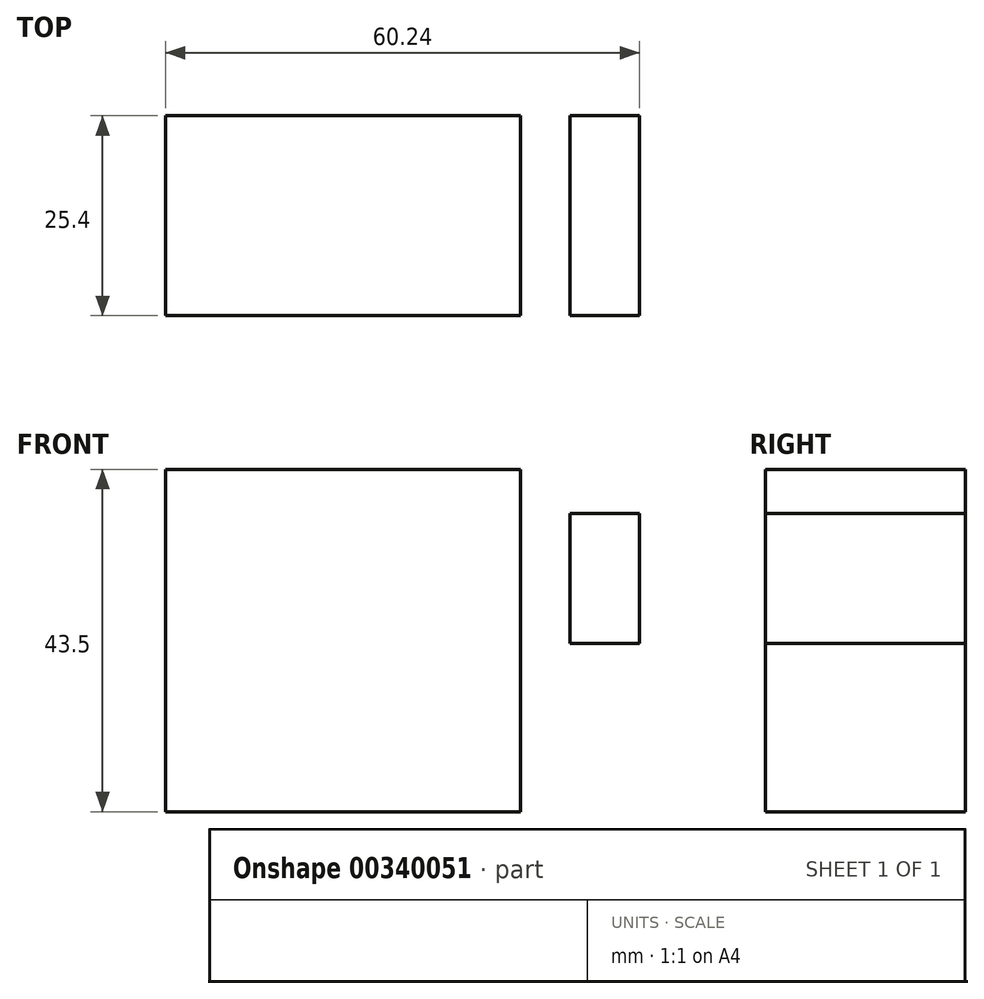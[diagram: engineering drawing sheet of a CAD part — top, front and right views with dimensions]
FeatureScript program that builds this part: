
annotation { "Feature Type Name" : "Feature", "Feature Type Description" : "" }
export const myFeature = defineFeature(function(context is Context, id is Id, definition is map)
    precondition{}
    {
        {
            var Q0;
            Q0=qCreatedBy(makeId("Front.planeOp"),FACE);
            var sketch = newSketch(context, id + "F0", { "sketchPlane" : qUnion([Q0])});
            skLineSegment(sketch, "E0.bottom", {"start": v(75.6, 76.06) * mm, "end": v(30.47, 76.06) * mm});
            skLineSegment(sketch, "E0.top", {"start": v(75.6, 32.56) * mm, "end": v(30.47, 32.56) * mm});
            skLineSegment(sketch, "E0.left", {"start": v(75.6, 76.06) * mm, "end": v(75.6, 32.56) * mm});
            skLineSegment(sketch, "E0.right", {"start": v(30.47, 76.06) * mm, "end": v(30.47, 32.56) * mm});
            skLineSegment(sketch, "E1.bottom", {"start": v(81.87, 53.96) * mm, "end": v(90.7, 53.96) * mm});
            skLineSegment(sketch, "E1.top", {"start": v(81.87, 70.47) * mm, "end": v(90.7, 70.47) * mm});
            skLineSegment(sketch, "E1.left", {"start": v(81.87, 53.96) * mm, "end": v(81.87, 70.47) * mm});
            skLineSegment(sketch, "E1.right", {"start": v(90.7, 53.96) * mm, "end": v(90.7, 70.47) * mm});
            skSolve(sketch);
        }
        {
            var Q0;
            Q0 = qSketchRegion(id + "F0", true);
            extrude(context, id + "F1", {"entities" : qUnion([Q0]), "depth" : 25.4 * mm});
        }
    });
